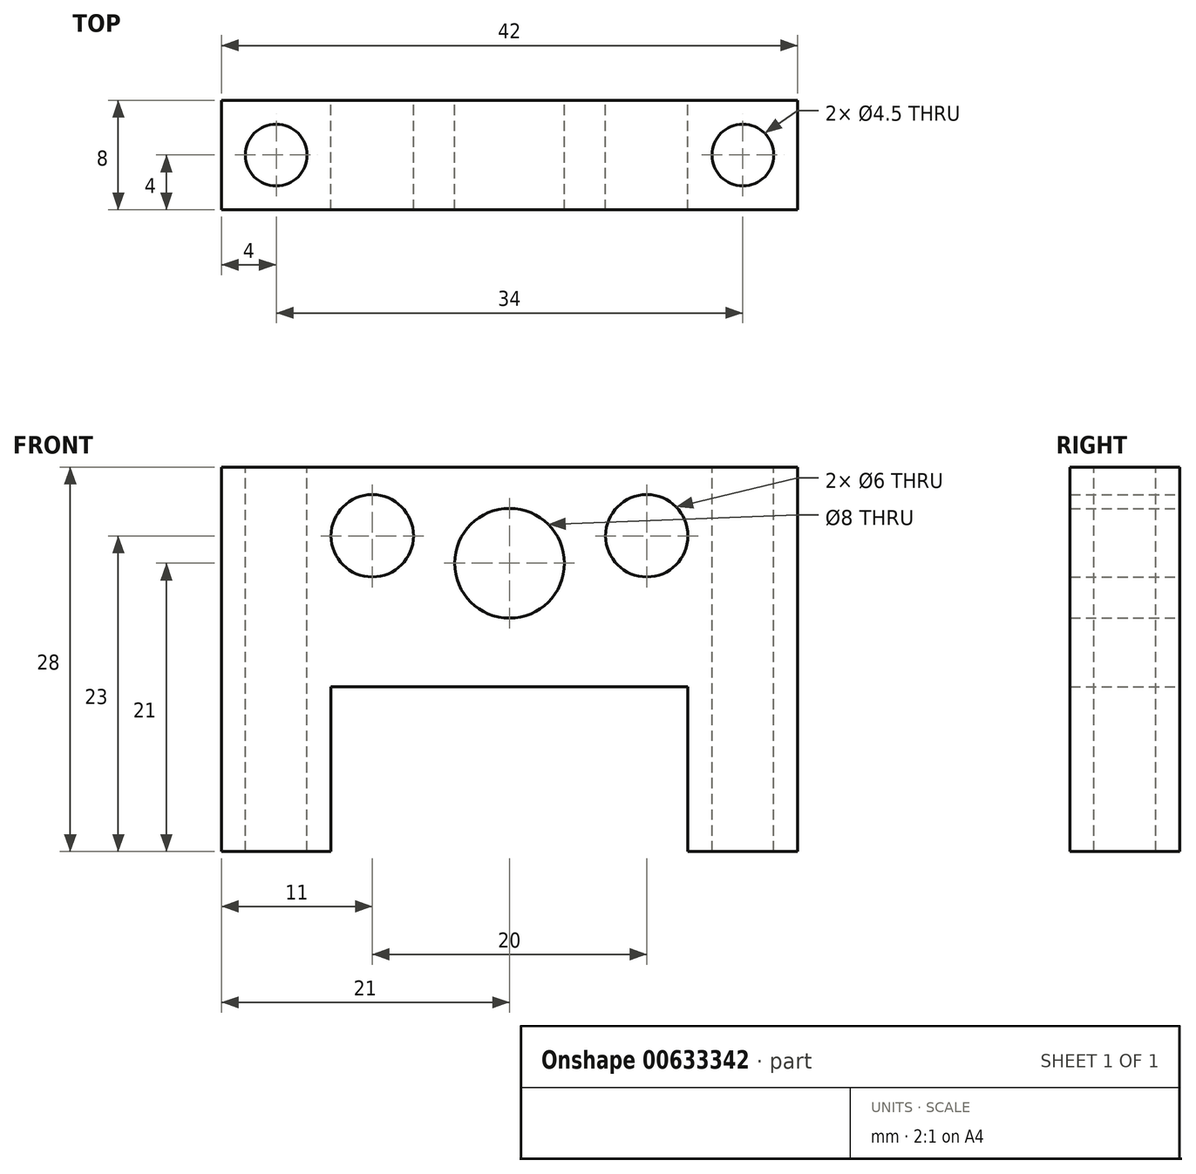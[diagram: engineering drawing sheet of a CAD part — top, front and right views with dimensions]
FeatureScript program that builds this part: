
annotation { "Feature Type Name" : "Feature", "Feature Type Description" : "" }
export const myFeature = defineFeature(function(context is Context, id is Id, definition is map)
    precondition{}
    {
        {
            var Q0;
            Q0=qCreatedBy(makeId("Front.planeOp"),FACE);
            var sketch = newSketch(context, id + "F0", { "sketchPlane" : qUnion([Q0])});
            skLineSegment(sketch, "E0.bottom", {"start": v(-21, 14) * mm, "end": v(21, 14) * mm});
            skLineSegment(sketch, "E0.top", {"start": v(-21, -14) * mm, "end": v(-13, -14) * mm});
            skLineSegment(sketch, "E0.left", {"start": v(-21, 14) * mm, "end": v(-21, -14) * mm});
            skLineSegment(sketch, "E0.right", {"start": v(21, 14) * mm, "end": v(21, -14) * mm});
            skPoint(sketch, "E0.middle", {"position": v(0, 0) * mm});
            skLineSegment(sketch, "E1.bottom", {"start": v(-13, -2) * mm, "end": v(13, -2) * mm});
            skLineSegment(sketch, "E1.left", {"start": v(-13, -2) * mm, "end": v(-13, -14) * mm});
            skLineSegment(sketch, "E1.right", {"start": v(13, -2) * mm, "end": v(13, -14) * mm});
            skLineSegment(sketch, "E2.trimOffspring", {"start": v(13, -14) * mm, "end": v(21, -14) * mm});
            skCircle(sketch, "E3", {"center": v(10, 9) * mm, "radius": 3 * mm});
            skCircle(sketch, "E4", {"center": v(0, 7) * mm, "radius": 4 * mm});
            skCircle(sketch, "E5.MirrorC", {"center": v(-10, 9) * mm, "radius": 3 * mm});
            skSolve(sketch);
        }
        {
            var Q0;
            Q0 = qSketchRegion(id + "F0", true);
            extrude(context, id + "F1", {"entities" : qUnion([Q0]), "depth" : 8 * mm, "offsetDistance" : 25 * mm});
        }
        {
            var Q0;
            Q0=makeQuery(id+"F1.opExtrude","SWEPT_FACE",FACE,{"disambiguationData":[OSD([sQuery(id+"F0.wireOp",EDGE,"E0.bottom")])]});
            var sketch = newSketch(context, id + "F2", { "sketchPlane" : qUnion([Q0])});
            skCircle(sketch, "E6", {"center": v(-17, -4) * mm, "radius": 2.25 * mm});
            skCircle(sketch, "E7.MirrorC", {"center": v(17, -4) * mm, "radius": 2.25 * mm});
            skSolve(sketch);
        }
        {
            var Q0;
            Q0 = qSketchRegion(id + "F2", true);
            extrude(context, id + "F3", {"entities" : qUnion([Q0]), "operationType" : NewBodyOperationType.REMOVE, "endBound" : BoundingType.THROUGH_ALL, "oppositeDirection" : true, "depth" : 25 * mm, "offsetDistance" : 25 * mm});
        }
    });
